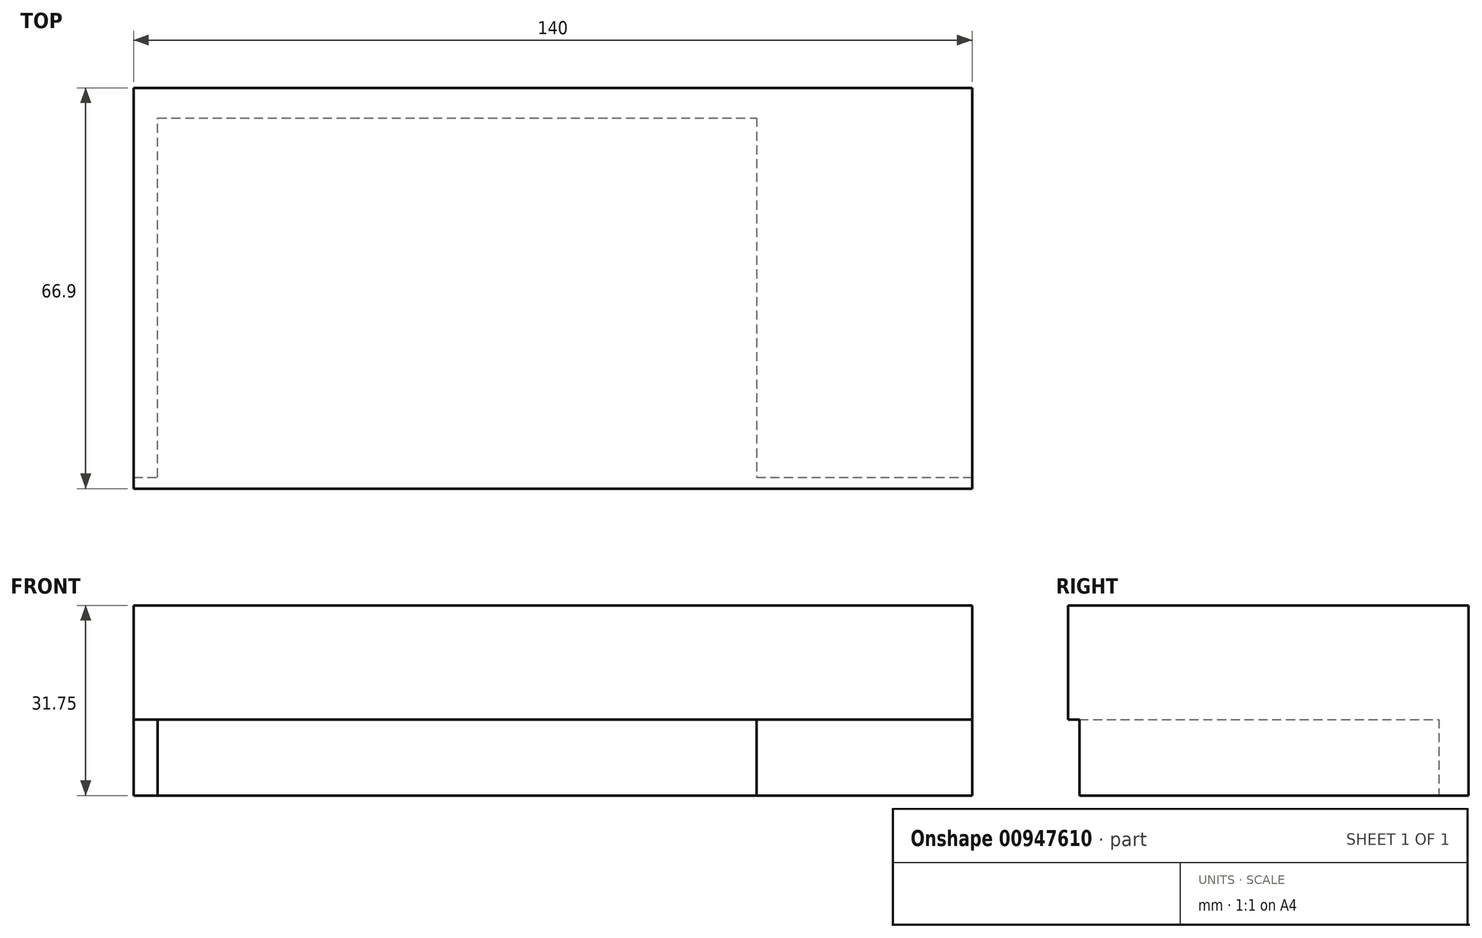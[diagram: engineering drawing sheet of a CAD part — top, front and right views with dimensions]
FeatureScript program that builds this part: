
annotation { "Feature Type Name" : "Feature", "Feature Type Description" : "" }
export const myFeature = defineFeature(function(context is Context, id is Id, definition is map)
    precondition{}
    {
        {
            var Q0;
            Q0=qCreatedBy(makeId("Front.planeOp"),FACE);
            var sketch = newSketch(context, id + "F0", { "sketchPlane" : qUnion([Q0])});
            skLineSegment(sketch, "E0.bottom", {"start": v(0, 0) * mm, "end": v(140, 0) * mm});
            skLineSegment(sketch, "E0.top", {"start": v(0, 31.75) * mm, "end": v(140, 31.75) * mm});
            skLineSegment(sketch, "E0.left", {"start": v(0, 0) * mm, "end": v(0, 31.75) * mm});
            skLineSegment(sketch, "E0.right", {"start": v(140, 0) * mm, "end": v(140, 31.75) * mm});
            skSolve(sketch);
        }
        {
            var Q0;
            Q0 = qSketchRegion(id + "F0", true);
            extrude(context, id + "F1", {"entities" : qUnion([Q0]), "depth" : 66.9 * mm, "offsetDistance" : 25.4 * mm});
        }
        {
            var Q0;
            Q0=makeQuery(id+"F1.opExtrude","SWEPT_FACE",FACE,{"disambiguationData":[OSD([sQuery(id+"F0.wireOp",EDGE,"E0.bottom")])]});
            var sketch = newSketch(context, id + "F2", { "sketchPlane" : qUnion([Q0])});
            skLineSegment(sketch, "E1", {"start": v(0, 65) * mm, "end": v(4, 65) * mm});
            skLineSegment(sketch, "E2", {"start": v(4, 65) * mm, "end": v(4, 5) * mm});
            skLineSegment(sketch, "E3", {"start": v(4, 5) * mm, "end": v(104, 5) * mm});
            skLineSegment(sketch, "E4", {"start": v(104, 5) * mm, "end": v(104, 65) * mm});
            skLineSegment(sketch, "E5", {"start": v(104, 65) * mm, "end": v(140, 65) * mm});
            skLineSegment(sketch, "E6", {"start": v(140, 65) * mm, "end": v(140, 66.9) * mm});
            skLineSegment(sketch, "E7", {"start": v(140, 66.9) * mm, "end": v(0, 66.9) * mm});
            skLineSegment(sketch, "E8", {"start": v(0, 66.9) * mm, "end": v(0, 65) * mm});
            skSolve(sketch);
        }
        {
            var Q0;
            Q0 = qSketchRegion(id + "F2", true);
            extrude(context, id + "F3", {"entities" : qUnion([Q0]), "operationType" : NewBodyOperationType.REMOVE, "oppositeDirection" : true, "depth" : 12.7 * mm, "offsetDistance" : 25 * mm});
        }
    });
